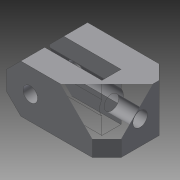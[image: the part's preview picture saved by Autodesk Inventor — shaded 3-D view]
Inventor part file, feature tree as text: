
AUTODESK INVENTOR PART (.ipt)
format: ipt  version: 2016 (Build 200138000, 138)  size: 141,824 bytes
history: native  units: mm
features: extrude x4, sketch x4, chamfer x2
ambient origin geometry x8: Origin, YZ Plane, XZ Plane, XY Plane, X Axis, Y Axis, Z Axis, Center Point
bodies: Solid1 (feature_tree)
feature tree (10):
  extrude  "Extrusion1"  Depth=10.0mm
  extrude  "Extrusion2"  Depth=12.0mm
  extrude  "Extrusion3"  Depth=20.0mm TaperAngle=0.0deg
  extrude  "Extrusion4"  Depth=20.0mm TaperAngle=0.0deg
  chamfer  "Chamfer1"  Distance=17.0mm
  chamfer  "Chamfer2"  Distance=6.1mm
  sketch  "Sketch1"  dims[d0=8.0mm d1=10.0mm]
  sketch  "Sketch2"  dims[d2=10.0mm d3=12.0mm]
  sketch  "Sketch3"  dims[d4=30.0mm d5=20.0mm d6=0.0mm]
  sketch  "Sketch4"  dims[d7=6.1mm d8=20.0mm d9=0.0mm d10=17.0mm d11=6.1mm d12=20.0mm d13=20.0mm d14=0.0mm d15=10.0mm d16=20.0mm d17=0.0mm d18=6.0mm d19=2.0mm d20=45.0deg d21=6.0mm d22=2.0mm d23=45.0deg d24=11.5mm d25=32.0mm]
